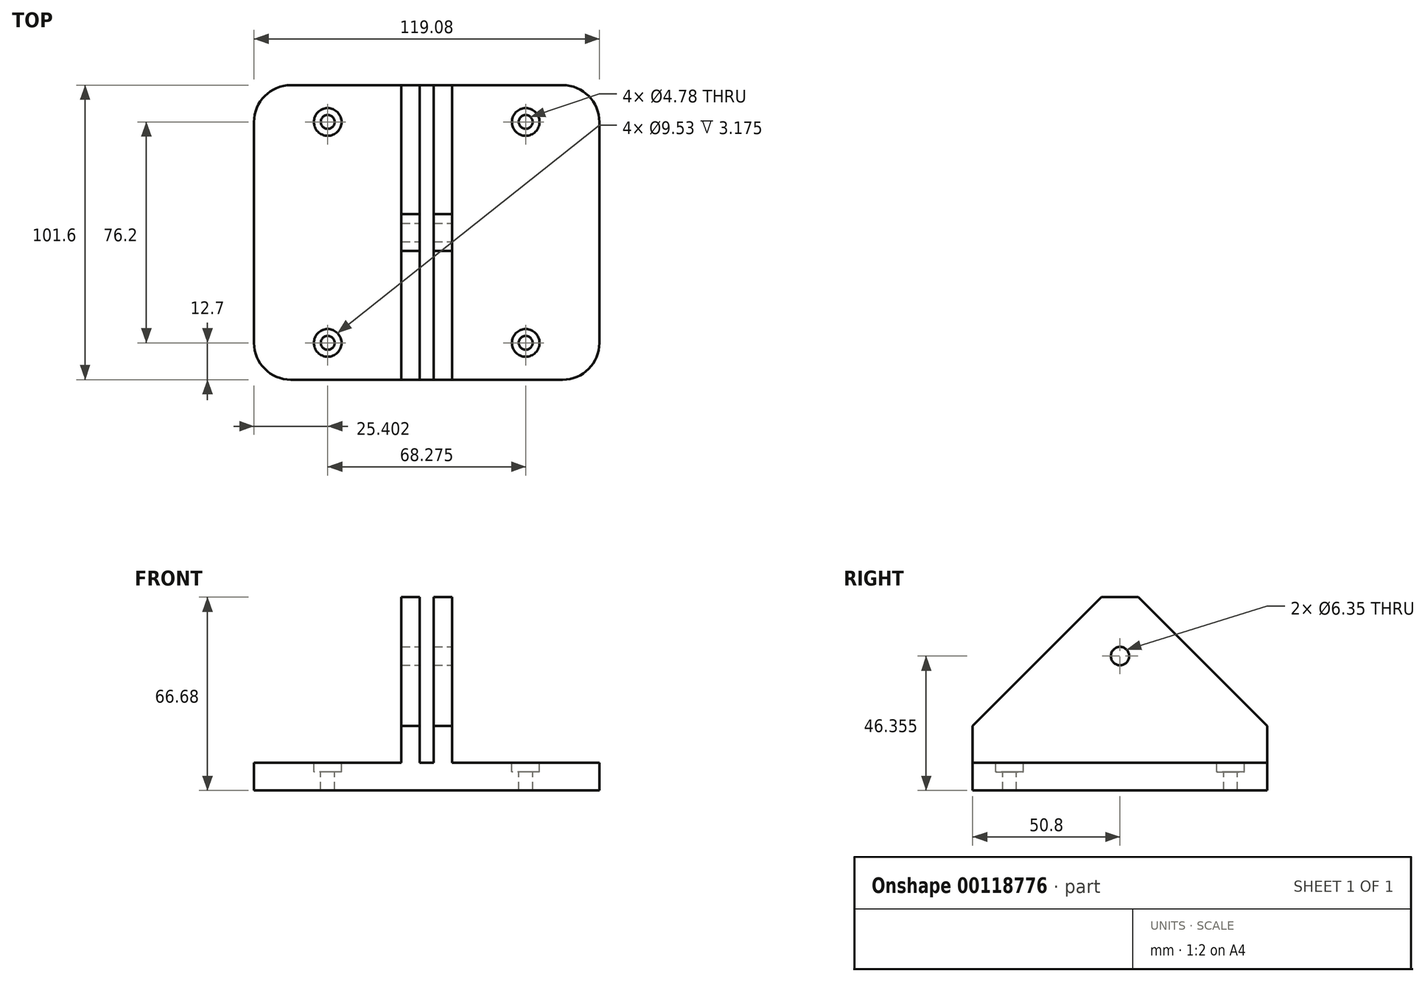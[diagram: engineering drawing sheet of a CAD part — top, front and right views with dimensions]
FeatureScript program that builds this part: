
annotation { "Feature Type Name" : "Feature", "Feature Type Description" : "" }
export const myFeature = defineFeature(function(context is Context, id is Id, definition is map)
    precondition{}
    {
        {
            var Q0;
            Q0=qCreatedBy(makeId("Front.planeOp"),FACE);
            var sketch = newSketch(context, id + "F0", { "sketchPlane" : qUnion([Q0])});
            skLineSegment(sketch, "E0.bottom", {"start": v(-78.6, -28.01) * mm, "end": v(-27.8, -28.01) * mm});
            skLineSegment(sketch, "E0.top", {"start": v(-78.6, -37.54) * mm, "end": v(40.48, -37.54) * mm});
            skLineSegment(sketch, "E0.left", {"start": v(-78.6, -28.01) * mm, "end": v(-78.6, -37.54) * mm});
            skLineSegment(sketch, "E0.right", {"start": v(40.48, -28.01) * mm, "end": v(40.48, -37.54) * mm});
            skLineSegment(sketch, "E1.top", {"start": v(-27.8, 29.14) * mm, "end": v(-21.45, 29.14) * mm});
            skLineSegment(sketch, "E1.left", {"start": v(-27.8, -28.01) * mm, "end": v(-27.8, 29.14) * mm});
            skLineSegment(sketch, "E1.right", {"start": v(-21.45, -28.01) * mm, "end": v(-21.45, 29.14) * mm});
            skLineSegment(sketch, "E2.top", {"start": v(-16.67, 29.14) * mm, "end": v(-10.32, 29.14) * mm});
            skLineSegment(sketch, "E2.left", {"start": v(-16.67, -28.01) * mm, "end": v(-16.67, 29.14) * mm});
            skLineSegment(sketch, "E2.right", {"start": v(-10.32, -28.01) * mm, "end": v(-10.32, 29.14) * mm});
            skLineSegment(sketch, "E3.trimOffspring", {"start": v(-21.45, -28.01) * mm, "end": v(-16.67, -28.01) * mm});
            skLineSegment(sketch, "E4.trimOffspring", {"start": v(-10.32, -28.01) * mm, "end": v(40.48, -28.01) * mm});
            skSolve(sketch);
        }
        {
            var Q0;
            Q0 = qSketchRegion(id + "F0", true);
            extrude(context, id + "F1", {"entities" : qUnion([Q0]), "depth" : 101.6 * mm});
        }
        {
            var Q0;
            Q0=makeQuery(id+"F1.opExtrude","SWEPT_FACE",FACE,{"disambiguationData":[OSD([sQuery(id+"F0.wireOp",EDGE,"E0.bottom")])]});
            var sketch = newSketch(context, id + "F2", { "sketchPlane" : qUnion([Q0])});
            skPoint(sketch, "E5", {"position": v(-53.2, -12.7) * mm});
            skPoint(sketch, "E5.positionSnap0", {"position": v(-53.2, 0) * mm});
            skPoint(sketch, "E6", {"position": v(-53.2, -88.9) * mm});
            skPoint(sketch, "E6.positionSnap0", {"position": v(-53.2, -101.6) * mm});
            skSolve(sketch);
        }
        {
            var Q0;
            Q0=sQuery(id+"F2.wireOp",VERTEX,"E5");
            var Q1;
            Q1=sQuery(id+"F2.wireOp",VERTEX,"E6");
            var Q2;
            Q2=makeQuery(id+"F1.opExtrude","SWEPT_BODY",BODY,{"disambiguationData":[OSD([sQuery(id+"F0.wireOp",EDGE,"E0.bottom"),sQuery(id+"F0.wireOp",EDGE,"E0.top"),sQuery(id+"F0.wireOp",EDGE,"E0.left"),sQuery(id+"F0.wireOp",EDGE,"E0.right"),sQuery(id+"F0.wireOp",EDGE,"E1.top"),sQuery(id+"F0.wireOp",EDGE,"E1.left"),sQuery(id+"F0.wireOp",EDGE,"E1.right"),sQuery(id+"F0.wireOp",EDGE,"E2.top"),sQuery(id+"F0.wireOp",EDGE,"E2.left"),sQuery(id+"F0.wireOp",EDGE,"E2.right"),sQuery(id+"F0.wireOp",EDGE,"E3.trimOffspring"),sQuery(id+"F0.wireOp",EDGE,"E4.trimOffspring")])]});
            hole(context, id + "F3", {"style" : HoleStyle.C_BORE, "endStyle" : HoleEndStyle.THROUGH, "holeDiameter" : 4.78 * mm, "cBoreDiameter" : 9.52 * mm, "cBoreDepth" : 3.17 * mm, "locations" : qUnion([Q0, Q1]), "scope" : qUnion([Q2]), "isTappedThrough" : true});
        }
        {
            var Q0;
            Q0=makeQuery(id+"F1.opExtrude","SWEPT_FACE",FACE,{"disambiguationData":[OSD([sQuery(id+"F0.wireOp",EDGE,"E4.trimOffspring")])]});
            var sketch = newSketch(context, id + "F4", { "sketchPlane" : qUnion([Q0])});
            skPoint(sketch, "E7", {"position": v(15.08, -88.9) * mm});
            skPoint(sketch, "E7.positionSnap0", {"position": v(15.08, -101.6) * mm});
            skPoint(sketch, "E8", {"position": v(15.08, -12.7) * mm});
            skPoint(sketch, "E8.positionSnap0", {"position": v(15.08, 0) * mm});
            skSolve(sketch);
        }
        {
            var Q0;
            Q0=sQuery(id+"F4.wireOp",VERTEX,"E7");
            var Q1;
            Q1=sQuery(id+"F4.wireOp",VERTEX,"E8");
            var Q2;
            Q2=makeQuery(id+"F1.opExtrude","SWEPT_BODY",BODY,{"disambiguationData":[OSD([sQuery(id+"F0.wireOp",EDGE,"E0.bottom"),sQuery(id+"F0.wireOp",EDGE,"E0.top"),sQuery(id+"F0.wireOp",EDGE,"E0.left"),sQuery(id+"F0.wireOp",EDGE,"E0.right"),sQuery(id+"F0.wireOp",EDGE,"E1.top"),sQuery(id+"F0.wireOp",EDGE,"E1.left"),sQuery(id+"F0.wireOp",EDGE,"E1.right"),sQuery(id+"F0.wireOp",EDGE,"E2.top"),sQuery(id+"F0.wireOp",EDGE,"E2.left"),sQuery(id+"F0.wireOp",EDGE,"E2.right"),sQuery(id+"F0.wireOp",EDGE,"E3.trimOffspring"),sQuery(id+"F0.wireOp",EDGE,"E4.trimOffspring")])]});
            hole(context, id + "F5", {"style" : HoleStyle.C_BORE, "endStyle" : HoleEndStyle.THROUGH, "holeDiameter" : 4.78 * mm, "cBoreDiameter" : 9.52 * mm, "cBoreDepth" : 3.17 * mm, "locations" : qUnion([Q0, Q1]), "scope" : qUnion([Q2]), "isTappedThrough" : true});
        }
        {
            var Q0;
            Q0=makeQuery(id+"F1.opExtrude","SWEPT_FACE",FACE,{"disambiguationData":[OSD([sQuery(id+"F0.wireOp",EDGE,"E2.right")])]});
            var sketch = newSketch(context, id + "F6", { "sketchPlane" : qUnion([Q0])});
            skPoint(sketch, "E9", {"position": v(-50.8, 8.82) * mm});
            skSolve(sketch);
        }
        {
            var Q0;
            Q0=sQuery(id+"F6.wireOp",VERTEX,"E9");
            var Q1;
            Q1=makeQuery(id+"F1.opExtrude","SWEPT_BODY",BODY,{"disambiguationData":[OSD([sQuery(id+"F0.wireOp",EDGE,"E0.bottom"),sQuery(id+"F0.wireOp",EDGE,"E0.top"),sQuery(id+"F0.wireOp",EDGE,"E0.left"),sQuery(id+"F0.wireOp",EDGE,"E0.right"),sQuery(id+"F0.wireOp",EDGE,"E1.top"),sQuery(id+"F0.wireOp",EDGE,"E1.left"),sQuery(id+"F0.wireOp",EDGE,"E1.right"),sQuery(id+"F0.wireOp",EDGE,"E2.top"),sQuery(id+"F0.wireOp",EDGE,"E2.left"),sQuery(id+"F0.wireOp",EDGE,"E2.right"),sQuery(id+"F0.wireOp",EDGE,"E3.trimOffspring"),sQuery(id+"F0.wireOp",EDGE,"E4.trimOffspring")])]});
            hole(context, id + "F7", {"style" : HoleStyle.SIMPLE, "endStyle" : HoleEndStyle.THROUGH, "holeDiameter" : 6.35 * mm, "locations" : qUnion([Q0]), "scope" : qUnion([Q1]), "isTappedThrough" : true});
        }
        {
            var Q0;
            Q0=makeQuery(id+"F1.opExtrude","CAP_EDGE",EDGE,{"disambiguationData":[OSD([sQuery(id+"F0.wireOp",EDGE,"E2.top")])],"isStart":false});
            var Q1;
            Q1=makeQuery(id+"F1.opExtrude","CAP_EDGE",EDGE,{"disambiguationData":[OSD([sQuery(id+"F0.wireOp",EDGE,"E1.top")])],"isStart":false});
            var Q2;
            Q2=makeQuery(id+"F1.opExtrude","CAP_EDGE",EDGE,{"disambiguationData":[OSD([sQuery(id+"F0.wireOp",EDGE,"E2.top")])],"isStart":true});
            var Q3;
            Q3=makeQuery(id+"F1.opExtrude","CAP_EDGE",EDGE,{"disambiguationData":[OSD([sQuery(id+"F0.wireOp",EDGE,"E1.top")])],"isStart":true});
            chamfer(context, id + "F8", {"entities" : qUnion([Q0, Q1, Q2, Q3]), "width" : 44.45 * mm, "tangentPropagation" : true});
        }
        {
            var Q0;
            Q0=makeQuery(id+"F1.opExtrude","CAP_EDGE",EDGE,{"disambiguationData":[OSD([sQuery(id+"F0.wireOp",EDGE,"E0.right")])],"isStart":false});
            var Q1;
            Q1=makeQuery(id+"F1.opExtrude","CAP_EDGE",EDGE,{"disambiguationData":[OSD([sQuery(id+"F0.wireOp",EDGE,"E0.right")])],"isStart":true});
            var Q2;
            Q2=makeQuery(id+"F1.opExtrude","CAP_EDGE",EDGE,{"disambiguationData":[OSD([sQuery(id+"F0.wireOp",EDGE,"E0.left")])],"isStart":false});
            var Q3;
            Q3=makeQuery(id+"F1.opExtrude","CAP_EDGE",EDGE,{"disambiguationData":[OSD([sQuery(id+"F0.wireOp",EDGE,"E0.left")])],"isStart":true});
            fillet(context, id + "F9", {"entities" : qUnion([Q0, Q1, Q2, Q3]), "radius" : 12.7 * mm, "tangentPropagation" : true, "allowEdgeOverflow" : false});
        }
    });
